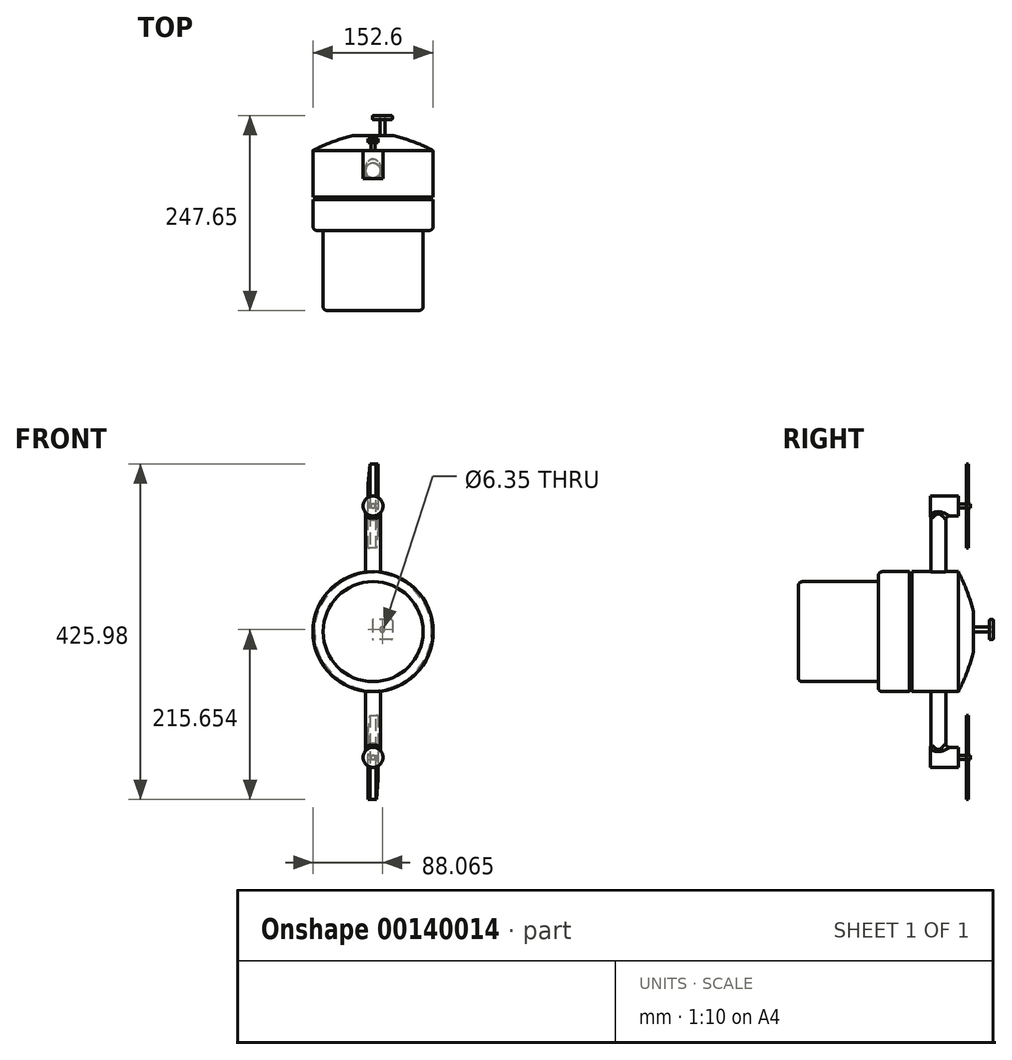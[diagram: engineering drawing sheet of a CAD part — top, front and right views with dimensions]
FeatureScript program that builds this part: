
annotation { "Feature Type Name" : "Feature", "Feature Type Description" : "" }
export const myFeature = defineFeature(function(context is Context, id is Id, definition is map)
    precondition{}
    {
        {
            var Q0;
            Q0=qCreatedBy(makeId("Front.planeOp"),FACE);
            var sketch = newSketch(context, id + "F0", { "sketchPlane" : qUnion([Q0])});
            skCircle(sketch, "E0", {"center": v(0, 0) * mm, "radius": 76.2 * mm});
            skSolve(sketch);
        }
        {
            var Q0;
            Q0=makeQuery(id+"F0.imprint","IMPRINT",FACE,{"disambiguationData":[TD([[makeQuery(id+"F0.imprint","IMPRINT",EDGE,{"derivedFrom":sQuery(id+"F0.wireOp",EDGE,"E0")}),1.0]])]});
            extrude(context, id + "F1", {"entities" : qUnion([Q0]), "depth" : 101.6 * mm});
        }
        {
            var Q0;
            Q0=qCreatedBy(makeId("Top.planeOp"),FACE);
            var sketch = newSketch(context, id + "F2", { "sketchPlane" : qUnion([Q0])});
            skCircle(sketch, "E1", {"center": v(0, -25.4) * mm, "radius": 9.53 * mm});
            skLineSegment(sketch, "E2", {"start": v(0, -101.6) * mm, "end": v(0, 0) * mm, "construction": true});
            skSolve(sketch);
        }
        {
            var Q0;
            Q0 = qSketchRegion(id + "F2", true);
            extrude(context, id + "F3", {"entities" : qUnion([Q0]), "operationType" : NewBodyOperationType.ADD, "depth" : 152.4 * mm});
        }
        {
            var Q0;
            Q0=qCreatedBy(makeId("Front.planeOp"),FACE);
            var sketch = newSketch(context, id + "F4", { "sketchPlane" : qUnion([Q0])});
            skCircle(sketch, "E3", {"center": v(0, 159.65) * mm, "radius": 12.7 * mm});
            skSolve(sketch);
        }
        {
            var Q0;
            Q0 = qSketchRegion(id + "F4", true);
            var Q1;
            Q1=makeQuery(id+"F3.opExtrude","SWEPT_FACE",FACE,{"disambiguationData":[OSD([sQuery(id+"F2.wireOp",EDGE,"E1")])]});
            extrude(context, id + "F5", {"entities" : qUnion([Q0]), "operationType" : NewBodyOperationType.ADD, "endBoundEntityFace" : qUnion([Q1]), "depth" : 35.56 * mm});
        }
        {
            var Q0;
            Q0=makeQuery(id+"F5.opExtrude","CAP_FACE",FACE,{"disambiguationData":[OSD([sQuery(id+"F4.wireOp",EDGE,"E3")])],"isStart":true});
            var sketch = newSketch(context, id + "F6", { "sketchPlane" : qUnion([Q0])});
            skCircle(sketch, "E4", {"center": v(0, 159.65) * mm, "radius": 2.54 * mm});
            skSolve(sketch);
        }
        {
            var Q0;
            Q0 = qSketchRegion(id + "F6", true);
            extrude(context, id + "F7", {"entities" : qUnion([Q0]), "operationType" : NewBodyOperationType.ADD, "depth" : 10.16 * mm});
        }
        {
            var Q0;
            Q0=qCreatedBy(makeId("Right.planeOp"),FACE);
            var sketch = newSketch(context, id + "F8", { "sketchPlane" : qUnion([Q0])});
            skLineSegment(sketch, "E5", {"start": v(10.1, 162.2) * mm, "end": v(10.16, 162.2) * mm});
            skLineSegment(sketch, "E6", {"start": v(15.24, 162.2) * mm, "end": v(15.24, 157.11) * mm});
            skLineSegment(sketch, "E7", {"start": v(15.24, 157.11) * mm, "end": v(12.7, 157.11) * mm});
            skLineSegment(sketch, "E8", {"start": v(10.16, 157.11) * mm, "end": v(10.16, 106.31) * mm});
            skLineSegment(sketch, "E9", {"start": v(10.16, 106.31) * mm, "end": v(12.7, 106.31) * mm});
            skLineSegment(sketch, "E10", {"start": v(12.7, 106.31) * mm, "end": v(12.7, 157.11) * mm});
            skLineSegment(sketch, "E11", {"start": v(0, 162.2) * mm, "end": v(10.1, 162.2) * mm, "construction": true});
            skLineSegment(sketch, "E12", {"start": v(10.16, 157.11) * mm, "end": v(0, 157.11) * mm, "construction": true});
            skLineSegment(sketch, "E13.0", {"start": v(10.16, 162.2) * mm, "end": v(10.16, 157.11) * mm});
            skPoint(sketch, "E14", {"position": v(10.16, 159.65) * mm});
            skPoint(sketch, "E15", {"position": v(15.24, 159.65) * mm});
            skLineSegment(sketch, "E16", {"start": v(15.24, 159.65) * mm, "end": v(10.16, 159.65) * mm, "construction": true});
            skLineSegment(sketch, "E17.MirrorCS", {"start": v(10.16, 162.2) * mm, "end": v(10.16, 213) * mm});
            skLineSegment(sketch, "E18.MirrorCS", {"start": v(12.7, 213) * mm, "end": v(12.7, 162.2) * mm});
            skLineSegment(sketch, "E19.MirrorCS", {"start": v(10.16, 213) * mm, "end": v(12.7, 213) * mm});
            skLineSegment(sketch, "E20.trimOffspring", {"start": v(12.7, 162.2) * mm, "end": v(15.24, 162.2) * mm});
            skSolve(sketch);
        }
        {
            var Q0;
            Q0 = qSketchRegion(id + "F8", true);
            extrude(context, id + "F9", {"entities" : qUnion([Q0]), "operationType" : NewBodyOperationType.ADD, "depth" : 6.35 * mm, "hasSecondDirection" : true, "secondDirectionOppositeDirection" : true, "secondDirectionDepth" : 6.35 * mm});
        }
        {
            var Q0;
            Q0=makeQuery(id+"F9.opExtrude","CAP_EDGE",EDGE,{"disambiguationData":[OSD([sQuery(id+"F8.wireOp",EDGE,"E9")])],"isStart":false});
            var Q1;
            Q1=makeQuery(id+"F9.opExtrude","CAP_EDGE",EDGE,{"disambiguationData":[OSD([sQuery(id+"F8.wireOp",EDGE,"E19.MirrorCS")])],"isStart":true});
            chamfer(context, id + "F10", {"entities" : qUnion([Q0, Q1]), "chamferType" : ChamferType.OFFSET_ANGLE, "width" : 25.4 * mm, "oppositeDirection" : false, "angle" : 5 * degree, "tangentPropagation" : true});
        }
        {
            var Q0;
            Q0=makeQuery(id+"F9.opExtrude","CAP_EDGE",EDGE,{"disambiguationData":[OSD([sQuery(id+"F8.wireOp",EDGE,"E8"),sQuery(id+"F8.wireOp",EDGE,"E13.0"),sQuery(id+"F8.wireOp",EDGE,"E17.MirrorCS")])],"isStart":true});
            var Q1;
            Q1=makeQuery(id+"F9.opExtrude","CAP_EDGE",EDGE,{"disambiguationData":[OSD([sQuery(id+"F8.wireOp",EDGE,"E8"),sQuery(id+"F8.wireOp",EDGE,"E13.0"),sQuery(id+"F8.wireOp",EDGE,"E17.MirrorCS")])],"isStart":false});
            chamfer(context, id + "F11", {"entities" : qUnion([Q0, Q1]), "chamferType" : ChamferType.OFFSET_ANGLE, "width" : 2.54 * mm, "oppositeDirection" : false, "angle" : 5 * degree, "tangentPropagation" : true});
        }
        {
            var Q0;
            Q0=makeQuery(id+"F1.opExtrude","SWEPT_BODY",BODY,{"disambiguationData":[OSD([sQuery(id+"F0.wireOp",EDGE,"E0")])]});
            var Q1;
            Q1=makeQuery(id+"F1.opExtrude","SWEPT_FACE",FACE,{"disambiguationData":[OSD([sQuery(id+"F0.wireOp",EDGE,"E0")])]});
            circularPattern(context, id + "F12", {"entities" : qUnion([Q0]), "axis" : qUnion([Q1]), "angle" : 360 * degree, "instanceCount" : 2, "equalSpace" : true});
        }
        {
            var Q0;
            Q0=qCreatedBy(makeId("Right.planeOp"),FACE);
            var sketch = newSketch(context, id + "F13", { "sketchPlane" : qUnion([Q0])});
            skLineSegment(sketch, "E21", {"start": v(0, 0) * mm, "end": v(19.05, 0) * mm});
            skLineSegment(sketch, "E22", {"start": v(0, 0) * mm, "end": v(0, -76.3) * mm});
            skArc(sketch, "E23", {"start": v(0, -76.3) * mm, "mid": v(11.1, -51.44) * mm, "end": v(19.05, -25.4) * mm});
            skLineSegment(sketch, "E24", {"start": v(19.05, 0) * mm, "end": v(19.05, -25.4) * mm});
            skSolve(sketch);
        }
        {
            var Q0;
            Q0=makeQuery(id+"F13.imprint","IMPRINT",FACE,{"disambiguationData":[TD([[makeQuery(id+"F13.imprint","IMPRINT",EDGE,{"derivedFrom":sQuery(id+"F13.wireOp",EDGE,"E21")}),-1.0]])]});
            var Q1;
            Q1=makeQuery(id+"F1.opExtrude","SWEPT_FACE",FACE,{"disambiguationData":[OSD([sQuery(id+"F0.wireOp",EDGE,"E0")])]});
            revolve(context, id + "F14", {"operationType" : NewBodyOperationType.ADD, "entities" : qUnion([Q0]), "axis" : qUnion([Q1]), "revolveType" : RevolveType.FULL});
        }
        {
            var Q0;
            Q0=makeQuery(id+"F14.opRevolve","SWEPT_EDGE",EDGE,{"disambiguationData":[OSD([sQuery(id+"F13.wireOp",EDGE,"E23"),sQuery(id+"F13.wireOp",EDGE,"E24")])]});
            fillet(context, id + "F15", {"entities" : qUnion([Q0]), "radius" : 5.08 * mm, "tangentPropagation" : true, "allowEdgeOverflow" : false});
        }
        {
            var Q0;
            Q0=makeQuery(id+"F1.opExtrude","CAP_FACE",FACE,{"disambiguationData":[OSD([sQuery(id+"F0.wireOp",EDGE,"E0")])],"isStart":false});
            var sketch = newSketch(context, id + "F16", { "sketchPlane" : qUnion([Q0])});
            skCircle(sketch, "E25", {"center": v(0, 0) * mm, "radius": 76.2 * mm});
            skSolve(sketch);
        }
        {
            var Q0;
            Q0=qCreatedBy(makeId("Right.planeOp"),FACE);
            var sketch = newSketch(context, id + "F17", { "sketchPlane" : qUnion([Q0])});
            skLineSegment(sketch, "E26.bottom", {"start": v(-58.82, 76.89) * mm, "end": v(-62.05, 76.89) * mm});
            skLineSegment(sketch, "E26.top", {"start": v(-58.82, 74.35) * mm, "end": v(-62.05, 74.35) * mm});
            skLineSegment(sketch, "E26.left", {"start": v(-58.82, 76.89) * mm, "end": v(-58.82, 74.35) * mm});
            skLineSegment(sketch, "E26.right", {"start": v(-62.05, 76.89) * mm, "end": v(-62.05, 74.35) * mm});
            skSolve(sketch);
        }
        {
            var Q0;
            Q0 = qSketchRegion(id + "F17", true);
            var Q1;
            Q1=sQuery(id+"F2.wireOp",EDGE,"E2");
            revolve(context, id + "F18", {"operationType" : NewBodyOperationType.REMOVE, "entities" : qUnion([Q0]), "axis" : qUnion([Q1]), "revolveType" : RevolveType.FULL, "oppositeDirection" : true});
        }
        {
            var Q0;
            Q0=makeQuery(id+"F16.imprint","IMPRINT",FACE,{"disambiguationData":[TD([[makeQuery(id+"F16.imprint","IMPRINT",EDGE,{"derivedFrom":sQuery(id+"F16.wireOp",EDGE,"E25")}),1.0]])]});
            var sketch = newSketch(context, id + "F19", { "sketchPlane" : qUnion([Q0])});
            skCircle(sketch, "E27", {"center": v(0, 0) * mm, "radius": 63.5 * mm});
            skSolve(sketch);
        }
        {
            var Q0;
            Q0=makeQuery(id+"F19.imprint","IMPRINT",FACE,{"disambiguationData":[TD([[makeQuery(id+"F19.imprint","IMPRINT",EDGE,{"derivedFrom":sQuery(id+"F19.wireOp",EDGE,"E27")}),1.0]])]});
            extrude(context, id + "F20", {"entities" : qUnion([Q0]), "operationType" : NewBodyOperationType.ADD, "depth" : 101.6 * mm});
        }
        {
            var Q0;
            Q0=makeQuery(id+"F14.opRevolve","SWEPT_FACE",FACE,{"disambiguationData":[OSD([sQuery(id+"F13.wireOp",EDGE,"E24")])]});
            var sketch = newSketch(context, id + "F21", { "sketchPlane" : qUnion([Q0])});
            skCircle(sketch, "E28", {"center": v(-11.76, 2.66) * mm, "radius": 3.18 * mm});
            skSolve(sketch);
        }
        {
            var Q0;
            Q0 = qSketchRegion(id + "F21", true);
            extrude(context, id + "F22", {"entities" : qUnion([Q0]), "operationType" : NewBodyOperationType.ADD, "depth" : 25.4 * mm});
        }
        {
            var Q0;
            Q0=makeQuery(id+"F22.opExtrude","CAP_FACE",FACE,{"disambiguationData":[OSD([sQuery(id+"F21.wireOp",EDGE,"E28")])],"isStart":false});
            var sketch = newSketch(context, id + "F23", { "sketchPlane" : qUnion([Q0])});
            skLineSegment(sketch, "E29.bottom", {"start": v(-24.46, 15.36) * mm, "end": v(0.94, 15.36) * mm});
            skLineSegment(sketch, "E29.top", {"start": v(-24.46, -10.04) * mm, "end": v(0.94, -10.04) * mm});
            skLineSegment(sketch, "E29.left", {"start": v(-24.46, 15.36) * mm, "end": v(-24.46, -10.04) * mm});
            skLineSegment(sketch, "E29.right", {"start": v(0.94, 15.36) * mm, "end": v(0.94, -10.04) * mm});
            skPoint(sketch, "E29.middle", {"position": v(-11.76, 2.66) * mm});
            skSolve(sketch);
        }
        {
            var Q0;
            Q0=makeQuery(id+"F23.imprint","IMPRINT",FACE,{"disambiguationData":[TD([[makeQuery(id+"F23.imprint","IMPRINT",EDGE,{"derivedFrom":sQuery(id+"F23.wireOp",EDGE,"E29.bottom")}),-1.0]])]});
            extrude(context, id + "F24", {"entities" : qUnion([Q0]), "oppositeDirection" : true, "depth" : 5.08 * mm});
        }
        {
            var Q0;
            Q0=makeQuery(id+"F24.opExtrude","CAP_FACE",FACE,{"disambiguationData":[OSD([sQuery(id+"F21.wireOp",EDGE,"E28"),sQuery(id+"F23.wireOp",EDGE,"E29.bottom"),sQuery(id+"F23.wireOp",EDGE,"E29.top"),sQuery(id+"F23.wireOp",EDGE,"E29.left"),sQuery(id+"F23.wireOp",EDGE,"E29.right")])],"isStart":true});
            var Q1;
            Q1=makeQuery(id+"F24.opExtrude","CAP_FACE",FACE,{"disambiguationData":[OSD([sQuery(id+"F21.wireOp",EDGE,"E28"),sQuery(id+"F23.wireOp",EDGE,"E29.bottom"),sQuery(id+"F23.wireOp",EDGE,"E29.top"),sQuery(id+"F23.wireOp",EDGE,"E29.left"),sQuery(id+"F23.wireOp",EDGE,"E29.right")])],"isStart":false});
            var Q2;
            Q2=makeQuery(id+"F24.opExtrude","SWEPT_EDGE",EDGE,{"disambiguationData":[OSD([sQuery(id+"F23.wireOp",EDGE,"E29.top"),sQuery(id+"F23.wireOp",EDGE,"E29.right")])]});
            var Q3;
            Q3=makeQuery(id+"F24.opExtrude","SWEPT_EDGE",EDGE,{"disambiguationData":[OSD([sQuery(id+"F23.wireOp",EDGE,"E29.bottom"),sQuery(id+"F23.wireOp",EDGE,"E29.right")])]});
            var Q4;
            Q4=makeQuery(id+"F24.opExtrude","SWEPT_EDGE",EDGE,{"disambiguationData":[OSD([sQuery(id+"F23.wireOp",EDGE,"E29.bottom"),sQuery(id+"F23.wireOp",EDGE,"E29.left")])]});
            var Q5;
            Q5=makeQuery(id+"F24.opExtrude","SWEPT_EDGE",EDGE,{"disambiguationData":[OSD([sQuery(id+"F23.wireOp",EDGE,"E29.top"),sQuery(id+"F23.wireOp",EDGE,"E29.left")])]});
            fillet(context, id + "F25", {"entities" : qUnion([Q0, Q1, Q2, Q3, Q4, Q5]), "radius" : 1.27 * mm, "tangentPropagation" : true, "allowEdgeOverflow" : false});
        }
        {
            var Q0;
            Q0=makeQuery(id+"F20.opExtrude","CAP_EDGE",EDGE,{"disambiguationData":[OSD([sQuery(id+"F19.wireOp",EDGE,"E27")])],"isStart":false});
            var Q1;
            Q1=makeQuery(id+"F1.opExtrude","CAP_EDGE",EDGE,{"disambiguationData":[OSD([sQuery(id+"F0.wireOp",EDGE,"E0")])],"isStart":false});
            var Q2;
            Q2=makeQuery(id+"F12.opPattern","COPY",EDGE,{"derivedFrom":makeQuery(id+"F5.boolean.opBoolean","INTERSECT",EDGE,{"derivedFrom":[makeQuery(id+"F3.opExtrude","SWEPT_FACE",FACE,{"disambiguationData":[OSD([sQuery(id+"F2.wireOp",EDGE,"E1")])]}),makeQuery(id+"F5.opExtrude","SWEPT_FACE",FACE,{"disambiguationData":[OSD([sQuery(id+"F4.wireOp",EDGE,"E3")])]})]}),"instanceName":"1"});
            var Q3;
            Q3=makeQuery(id+"F5.boolean.opBoolean","INTERSECT",EDGE,{"derivedFrom":[makeQuery(id+"F3.opExtrude","SWEPT_FACE",FACE,{"disambiguationData":[OSD([sQuery(id+"F2.wireOp",EDGE,"E1")])]}),makeQuery(id+"F5.opExtrude","SWEPT_FACE",FACE,{"disambiguationData":[OSD([sQuery(id+"F4.wireOp",EDGE,"E3")])]})]});
            fillet(context, id + "F26", {"entities" : qUnion([Q0, Q1, Q2, Q3]), "radius" : 5.08 * mm, "tangentPropagation" : true, "allowEdgeOverflow" : false});
        }
    });
